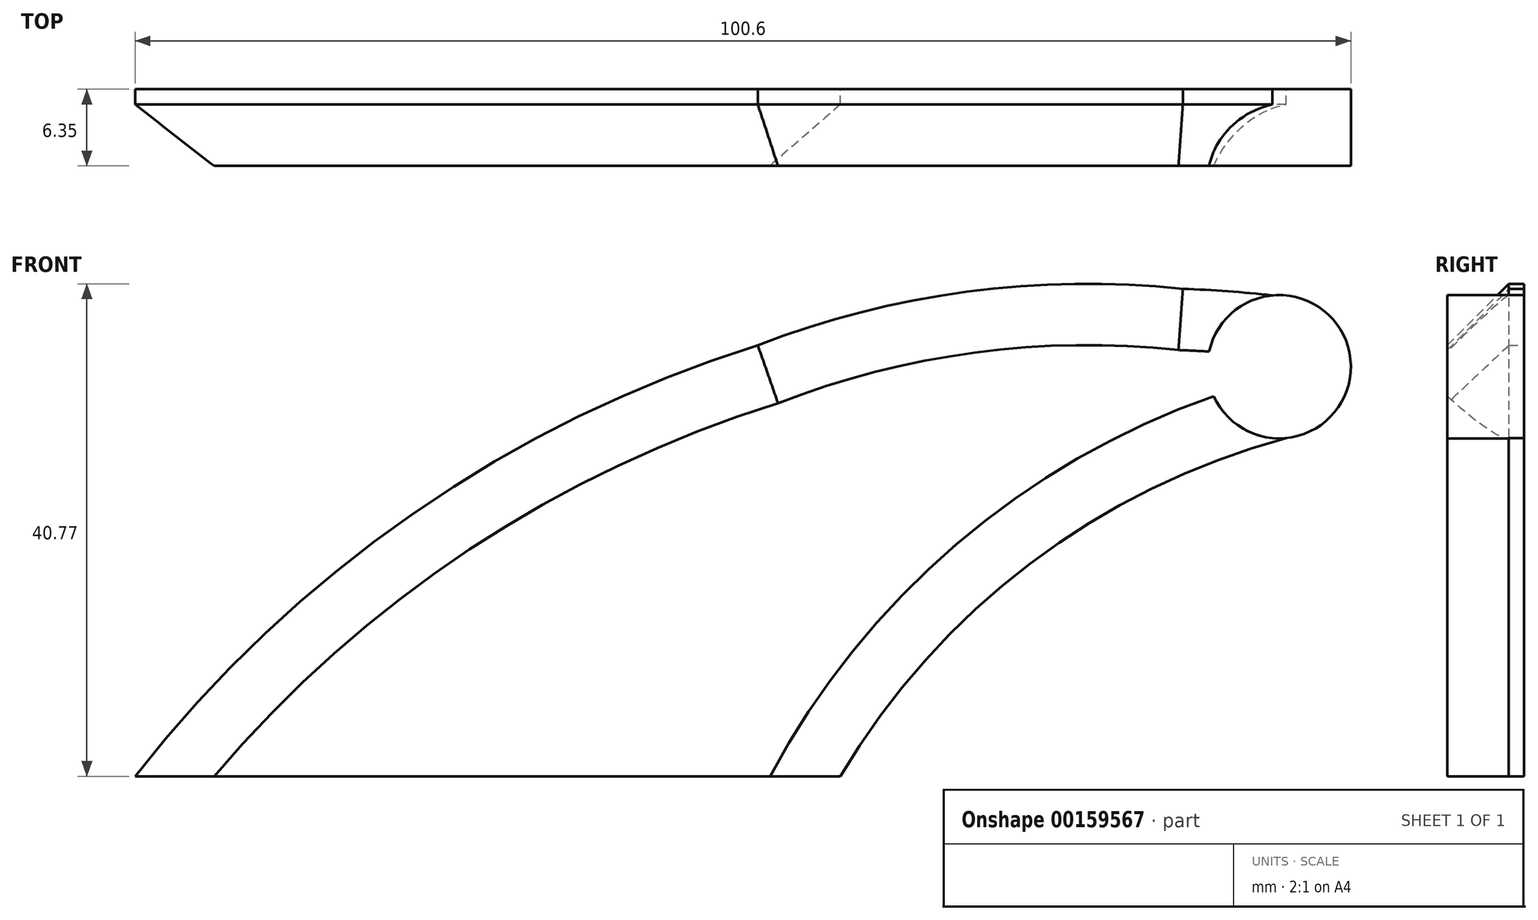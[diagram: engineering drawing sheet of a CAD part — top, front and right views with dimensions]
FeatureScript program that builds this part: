
annotation { "Feature Type Name" : "Feature", "Feature Type Description" : "" }
export const myFeature = defineFeature(function(context is Context, id is Id, definition is map)
    precondition{}
    {
        {
            var Q0;
            Q0=qCreatedBy(makeId("Front.planeOp"),FACE);
            var sketch = newSketch(context, id + "F0", { "sketchPlane" : qUnion([Q0])});
            skLineSegment(sketch, "E0", {"start": v(9.36, -33.9) * mm, "end": v(-49, -33.9) * mm});
            skCircle(sketch, "E1", {"center": v(45.67, 0) * mm, "radius": 5.93 * mm});
            skArc(sketch, "E2", {"start": v(45.12, 5.9) * mm, "mid": v(-7.11, -1.76) * mm, "end": v(-49, -33.9) * mm});
            skArc(sketch, "E3", {"start": v(-12.3, -4.11) * mm, "mid": v(-27.16, -13.45) * mm, "end": v(-40.77, -24.54) * mm});
            skArc(sketch, "E4", {"start": v(37.7, 6.45) * mm, "mid": v(19.83, 6.21) * mm, "end": v(2.53, 1.77) * mm});
            skArc(sketch, "E5", {"start": v(46.25, -5.9) * mm, "mid": v(25.06, -16.3) * mm, "end": v(9.36, -33.9) * mm});
            skArc(sketch, "E6", {"start": v(39.41, -8.18) * mm, "mid": v(23.63, -16.88) * mm, "end": v(11.64, -30.34) * mm});
            skSolve(sketch);
        }
        {
            var Q0;
            {var subQ0=sQuery(id+"F0.wireOp",EDGE,"E1");var subQ1=makeQuery(id+"F0.imprint","INTERSECT",VERTEX,{"derivedFrom":[subQ0,sQuery(id+"F0.wireOp",EDGE,"E2")]});Q0=makeQuery(id+"F0.imprint","IMPRINT",FACE,{"disambiguationData":[TD([[makeQuery(id+"F0.imprint","IMPRINT",EDGE,{"disambiguationData":[TD([[subQ1,-1.0]])],"derivedFrom":subQ0}),1.0]])]});}
            var Q1;
            {var subQ0=sQuery(id+"F0.wireOp",EDGE,"E4");Q1=makeQuery(id+"F0.imprint","IMPRINT",FACE,{"disambiguationData":[TD([[makeQuery(id+"F0.imprint","IMPRINT",EDGE,{"derivedFrom":subQ0}),1.0]])]});}
            var Q2;
            {var subQ0=sQuery(id+"F0.wireOp",EDGE,"E3");Q2=makeQuery(id+"F0.imprint","IMPRINT",FACE,{"disambiguationData":[TD([[makeQuery(id+"F0.imprint","IMPRINT",EDGE,{"derivedFrom":subQ0}),-1.0]])]});}
            var Q3;
            {var subQ0=sQuery(id+"F0.wireOp",EDGE,"E6");Q3=makeQuery(id+"F0.imprint","IMPRINT",FACE,{"disambiguationData":[TD([[makeQuery(id+"F0.imprint","IMPRINT",EDGE,{"derivedFrom":subQ0}),1.0]])]});}
            var Q4;
            {var subQ10=sQuery(id+"F0.wireOp",EDGE,"E0");Q4=makeQuery(id+"F0.imprint","IMPRINT",FACE,{"disambiguationData":[TD([[makeQuery(id+"F0.imprint","IMPRINT",EDGE,{"derivedFrom":subQ10}),-1.0]])]});}
            extrude(context, id + "F1", {"entities" : qUnion([Q0, Q1, Q2, Q3, Q4]), "depth" : 6.35 * mm});
        }
        {
            var Q0;
            Q0=makeQuery(id+"F1.opExtrude","CAP_EDGE",EDGE,{"disambiguationData":[OSD([sQuery(id+"F0.wireOp",EDGE,"E4")])],"isStart":false});
            var Q1;
            Q1=makeQuery(id+"F1.opExtrude","CAP_EDGE",EDGE,{"disambiguationData":[OSD([sQuery(id+"F0.wireOp",EDGE,"E5")])],"isStart":false});
            chamfer(context, id + "F2", {"entities" : qUnion([Q0, Q1]), "width" : 5.08 * mm, "tangentPropagation" : true});
        }
    });
